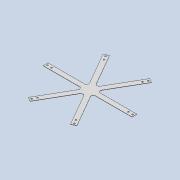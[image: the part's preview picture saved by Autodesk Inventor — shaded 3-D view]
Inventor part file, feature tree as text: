
AUTODESK INVENTOR PART (.ipt)
format: ipt  version: 2020 (Build 240168000, 168)  size: 200,192 bytes
history: native  units: mm
features: extrude x3, sketch x3, projected_geometry x2, fillet x1, pattern_circular x1
ambient origin geometry x8: Origin, YZ Plane, XZ Plane, XY Plane, X Axis, Y Axis, Z Axis, Center Point
bodies: Solid1 (feature_tree)
feature tree (10):
  extrude  "Extrusion1"  Depth=100.0mm
  extrude  "Extrusion2"  Depth=0.2mm
  fillet  "Fillet1"  Radius=50.0mm
  extrude  "Extrusion3"  Depth=0.2mm
  pattern_circular  "Circular Pattern1"  [2 undecoded]
  sketch  "Sketch1"  dims[d0=100.0mm d1=100.0mm]
  sketch  "Sketch2"  dims[d2=0.2mm d3=0.0mm d4=50.0mm d5=50.0mm]
  projected_geometry  "Projected Loop1"
  sketch  "Sketch3"  dims[d6=12.0mm d7=27.0mm d8=4.0mm d9=27.0mm d10=5.0mm d11=4.0mm d12=10.0mm d13=60.0mm d15=360.0deg d17=0.2mm d18=0.0mm d19=1.0mm d20=32.0mm d21=3.5mm d22=1.2mm d23=1.2mm d24=0.2mm d25=0.0mm d26=60.0mm d27=360.0deg]
  projected_geometry  "Projected Loop2"
note: 2 required parameter values undecoded (feature->parameter linkage not recoverable at this tier; creation-order binding heuristic only, values carry confidence <= 0.55)
